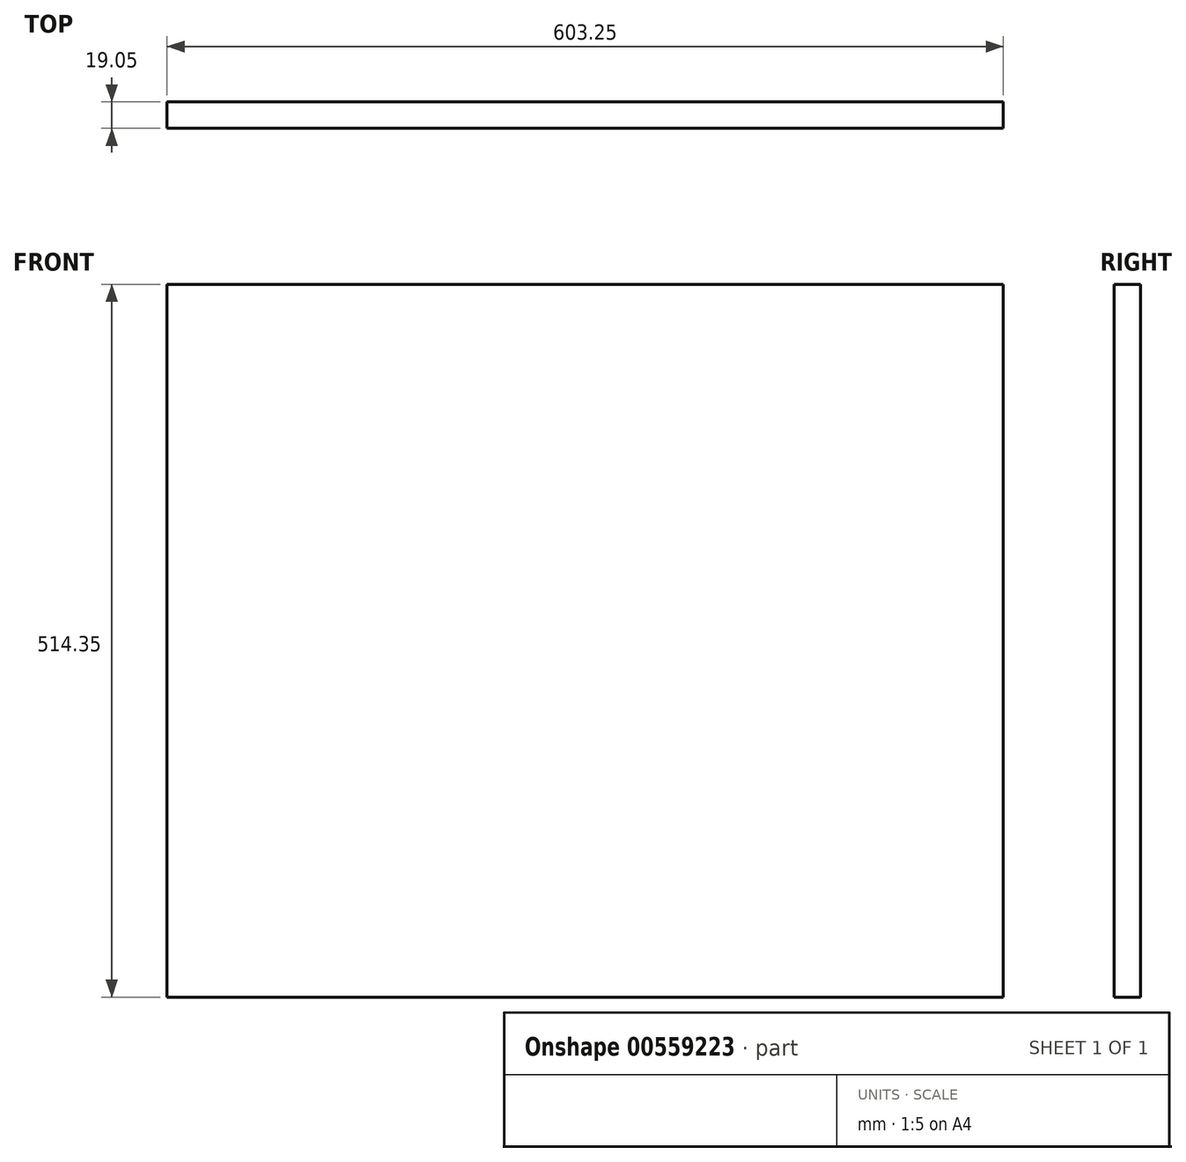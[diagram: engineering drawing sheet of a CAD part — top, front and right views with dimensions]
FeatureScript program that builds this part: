
annotation { "Feature Type Name" : "Feature", "Feature Type Description" : "" }
export const myFeature = defineFeature(function(context is Context, id is Id, definition is map)
    precondition{}
    {
        {
            var Q0;
            Q0=qCreatedBy(makeId("Front.planeOp"),FACE);
            var sketch = newSketch(context, id + "F0", { "sketchPlane" : qUnion([Q0])});
            skLineSegment(sketch, "E0.bottom", {"start": v(0, 0) * mm, "end": v(603.25, 0) * mm});
            skLineSegment(sketch, "E0.top", {"start": v(0, 514.35) * mm, "end": v(603.25, 514.35) * mm});
            skLineSegment(sketch, "E0.left", {"start": v(0, 0) * mm, "end": v(0, 514.35) * mm});
            skLineSegment(sketch, "E0.right", {"start": v(603.25, 0) * mm, "end": v(603.25, 514.35) * mm});
            skSolve(sketch);
        }
        {
            var Q0;
            Q0=makeQuery(id+"F0.imprint","IMPRINT",FACE,{"disambiguationData":[TD([[makeQuery(id+"F0.imprint","IMPRINT",EDGE,{"derivedFrom":sQuery(id+"F0.wireOp",EDGE,"E0.bottom")}),1.0]])]});
            extrude(context, id + "F1", {"entities" : qUnion([Q0]), "depth" : 19.05 * mm, "offsetDistance" : 25.4 * mm});
        }
    });
